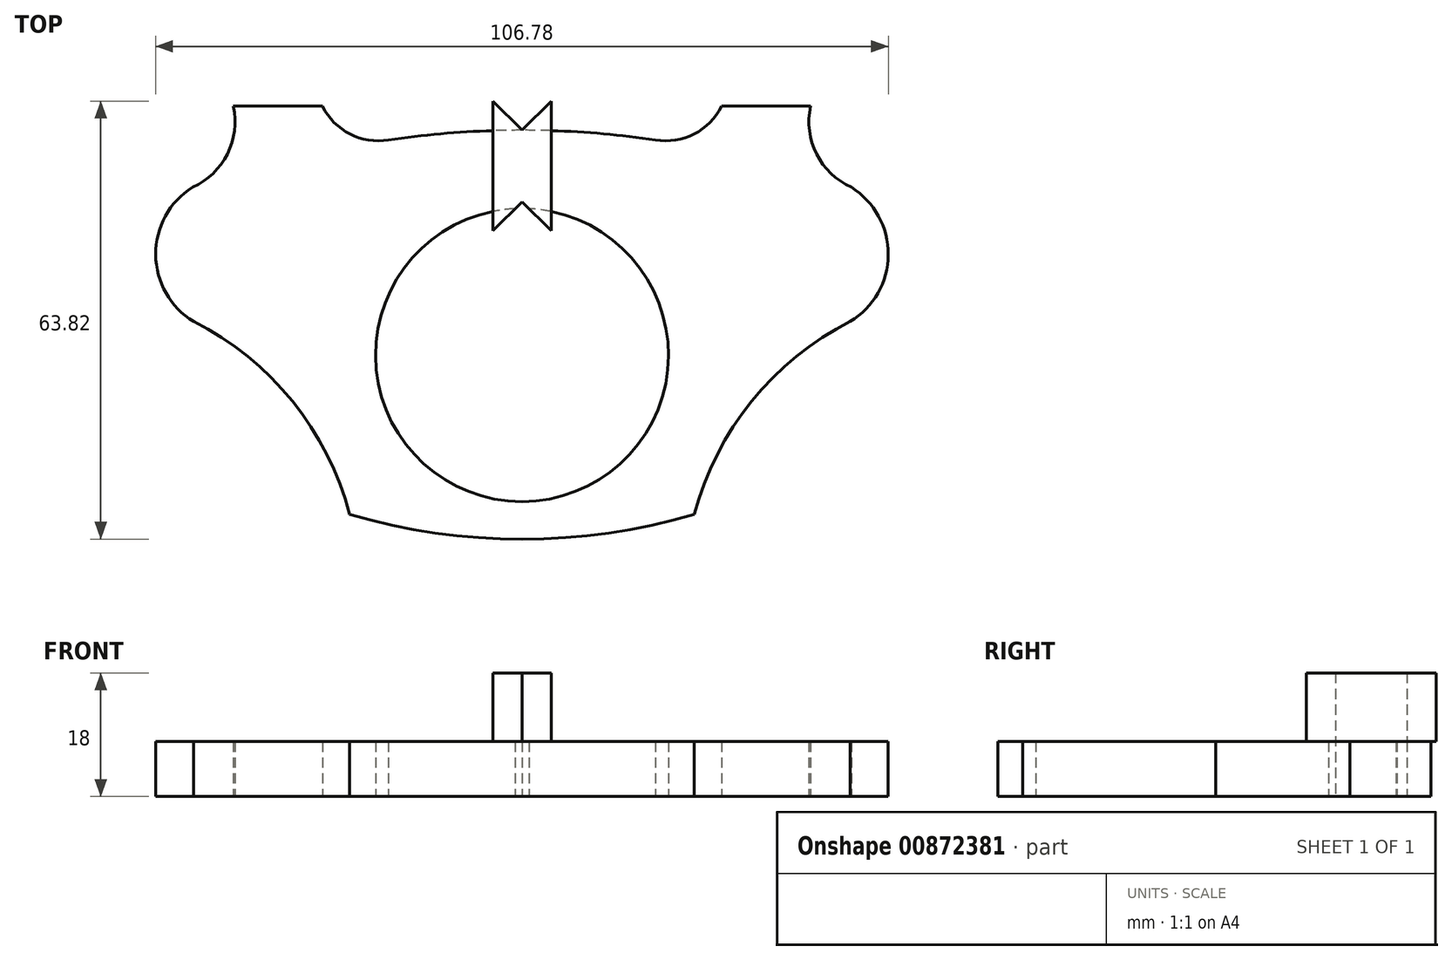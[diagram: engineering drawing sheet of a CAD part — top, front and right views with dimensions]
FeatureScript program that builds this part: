
annotation { "Feature Type Name" : "Feature", "Feature Type Description" : "" }
export const myFeature = defineFeature(function(context is Context, id is Id, definition is map)
    precondition{}
    {
        {
            var Q0;
            Q0=qCreatedBy(makeId("Top.planeOp"),FACE);
            var sketch = newSketch(context, id + "F0", { "sketchPlane" : qUnion([Q0])});
            skLineSegment(sketch, "E0", {"start": v(29.08, 21.54) * mm, "end": v(42.07, 21.54) * mm});
            skArc(sketch, "E1", {"start": v(0, -36.07) * mm, "mid": v(21.35, -14.72) * mm, "end": v(0, 6.63) * mm});
            skArc(sketch, "E2", {"start": v(46.62, -10.48) * mm, "mid": v(53.39, -0.01) * mm, "end": v(46.64, 10.47) * mm});
            skArc(sketch, "E3", {"start": v(47.85, -9.84) * mm, "mid": v(33.47, -21.45) * mm, "end": v(25.12, -37.94) * mm});
            skArc(sketch, "E4", {"start": v(42.07, 21.54) * mm, "mid": v(42.93, 14.58) * mm, "end": v(48, 9.74) * mm});
            skArc(sketch, "E5.trimOffspring", {"start": v(45.5, -29.1) * mm, "mid": v(45.96, -28.82) * mm, "end": v(46.44, -28.53) * mm});
            skArc(sketch, "E6", {"start": v(19.84, 16.57) * mm, "mid": v(9.95, 17.67) * mm, "end": v(0, 18.04) * mm});
            skArc(sketch, "E7", {"start": v(19.45, 16.63) * mm, "mid": v(25.08, 17.49) * mm, "end": v(29.08, 21.54) * mm});
            skLineSegment(sketch, "E8", {"start": v(0, 47.81) * mm, "end": v(0, -44.36) * mm, "construction": true});
            skArc(sketch, "E9.trimOffspring", {"start": v(0, -41.54) * mm, "mid": v(12.69, -40.64) * mm, "end": v(25.12, -37.94) * mm});
            skArc(sketch, "E10.MirrorCS", {"start": v(-19.84, 16.57) * mm, "mid": v(-9.95, 17.67) * mm, "end": v(0, 18.04) * mm});
            skArc(sketch, "E11.MirrorCS", {"start": v(-19.45, 16.63) * mm, "mid": v(-25.08, 17.49) * mm, "end": v(-29.08, 21.54) * mm});
            skLineSegment(sketch, "E12.MirrorCS", {"start": v(-29.08, 21.54) * mm, "end": v(-42.07, 21.54) * mm});
            skArc(sketch, "E13.MirrorCS", {"start": v(-42.07, 21.54) * mm, "mid": v(-42.93, 14.58) * mm, "end": v(-48, 9.74) * mm});
            skArc(sketch, "E14.MirrorCS", {"start": v(-46.62, -10.48) * mm, "mid": v(-53.39, -0.01) * mm, "end": v(-46.64, 10.47) * mm});
            skArc(sketch, "E15.MirrorCS", {"start": v(-47.85, -9.84) * mm, "mid": v(-33.47, -21.45) * mm, "end": v(-25.12, -37.94) * mm});
            skArc(sketch, "E16.MirrorCS", {"start": v(0, -41.54) * mm, "mid": v(-12.69, -40.64) * mm, "end": v(-25.12, -37.94) * mm});
            skArc(sketch, "E17.MirrorCS", {"start": v(0, -36.07) * mm, "mid": v(-21.35, -14.72) * mm, "end": v(0, 6.63) * mm});
            skSolve(sketch);
        }
        {
            var Q0;
            {var subQ9=sQuery(id+"F0.wireOp",EDGE,"E0");Q0=makeQuery(id+"F0.imprint","IMPRINT",FACE,{"disambiguationData":[TD([[makeQuery(id+"F0.imprint","IMPRINT",EDGE,{"derivedFrom":subQ9}),-1.0]])]});}
            extrude(context, id + "F1", {"entities" : qUnion([Q0]), "depth" : 8 * mm, "offsetDistance" : 25 * mm});
        }
        {
            var Q0;
            Q0=makeQuery(id+"F1.opExtrude","CAP_FACE",FACE,{"disambiguationData":[OSD([sQuery(id+"F0.wireOp",EDGE,"E0"),sQuery(id+"F0.wireOp",EDGE,"E1"),sQuery(id+"F0.wireOp",EDGE,"E2"),sQuery(id+"F0.wireOp",EDGE,"E3"),sQuery(id+"F0.wireOp",EDGE,"E4"),sQuery(id+"F0.wireOp",EDGE,"E6"),sQuery(id+"F0.wireOp",EDGE,"E7"),sQuery(id+"F0.wireOp",EDGE,"E9.trimOffspring"),sQuery(id+"F0.wireOp",EDGE,"E10.MirrorCS"),sQuery(id+"F0.wireOp",EDGE,"E11.MirrorCS"),sQuery(id+"F0.wireOp",EDGE,"E12.MirrorCS"),sQuery(id+"F0.wireOp",EDGE,"E13.MirrorCS"),sQuery(id+"F0.wireOp",EDGE,"E14.MirrorCS"),sQuery(id+"F0.wireOp",EDGE,"E15.MirrorCS"),sQuery(id+"F0.wireOp",EDGE,"E16.MirrorCS"),sQuery(id+"F0.wireOp",EDGE,"E17.MirrorCS")])],"isStart":false});
            var sketch = newSketch(context, id + "F2", { "sketchPlane" : qUnion([Q0])});
            skLineSegment(sketch, "E18.0", {"start": v(0, 7.62) * mm, "end": v(4.24, 3.38) * mm});
            skLineSegment(sketch, "E18.3", {"start": v(-4.24, 3.38) * mm, "end": v(0, 7.62) * mm});
            skPoint(sketch, "E18.0.midPoint", {"position": v(2.12, 5.5) * mm});
            skLineSegment(sketch, "E19", {"start": v(0, 7.62) * mm, "end": v(0, 7.62) * mm});
            skLineSegment(sketch, "E20.1", {"start": v(4.24, 22.28) * mm, "end": v(0, 18.04) * mm});
            skLineSegment(sketch, "E20.2", {"start": v(0, 18.04) * mm, "end": v(-4.24, 22.28) * mm});
            skPoint(sketch, "E20.0.midPoint", {"position": v(2.12, 23.34) * mm});
            skLineSegment(sketch, "E21", {"start": v(-4.24, 22.28) * mm, "end": v(-4.24, 3.38) * mm});
            skLineSegment(sketch, "E22", {"start": v(4.24, 3.38) * mm, "end": v(4.24, 22.28) * mm});
            skPoint(sketch, "E20.3.end.orphan", {"position": v(0, 24.4) * mm});
            skPoint(sketch, "E23.orphan", {"position": v(0, 11.07) * mm});
            skPoint(sketch, "E20.cCircle.center.orphan", {"position": v(0, 20.15) * mm});
            skPoint(sketch, "E18.cCircle.center.orphan", {"position": v(0, 4.66) * mm});
            skSolve(sketch);
        }
        {
            var Q0;
            Q0 = qSketchRegion(id + "F2", true);
            extrude(context, id + "F3", {"entities" : qUnion([Q0]), "operationType" : NewBodyOperationType.ADD, "depth" : 10 * mm, "offsetDistance" : 25 * mm});
        }
        {
            var Q0;
            Q0=makeQuery(id+"F3.opExtrude","CAP_FACE",FACE,{"disambiguationData":[OSD([sQuery(id+"F2.wireOp",EDGE,"E18.0"),sQuery(id+"F2.wireOp",EDGE,"E18.3"),sQuery(id+"F2.wireOp",EDGE,"E20.1"),sQuery(id+"F2.wireOp",EDGE,"E20.2"),sQuery(id+"F2.wireOp",EDGE,"E21"),sQuery(id+"F2.wireOp",EDGE,"E22")])],"isStart":false});
            var sketch = newSketch(context, id + "F4", { "sketchPlane" : qUnion([Q0])});
            skLineSegment(sketch, "E24", {"start": v(0, 7.62) * mm, "end": v(-4.24, 3.38) * mm});
            skLineSegment(sketch, "E25", {"start": v(-4.24, 3.38) * mm, "end": v(4.24, 3.38) * mm});
            skLineSegment(sketch, "E26", {"start": v(4.24, 3.38) * mm, "end": v(0, 7.62) * mm});
            skSolve(sketch);
        }
        {
            var Q0;
            Q0 = qSketchRegion(id + "F4", true);
            extrude(context, id + "F5", {"entities" : qUnion([Q0]), "operationType" : NewBodyOperationType.REMOVE, "oppositeDirection" : true, "depth" : 25 * mm, "offsetDistance" : 25 * mm});
        }
    });
